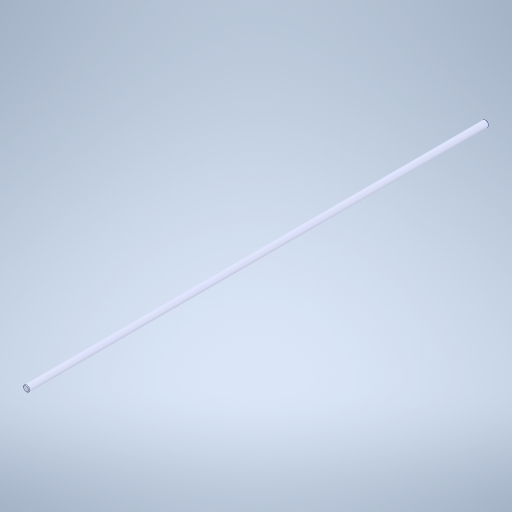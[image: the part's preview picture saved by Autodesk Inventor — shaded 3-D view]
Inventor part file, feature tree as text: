
AUTODESK INVENTOR PART (.ipt)
format: ipt  version: 2023 (Build 270158000, 158)  size: 261,120 bytes
history: mixed  units: in
note: dims shown in document units (in); Inventor stores cm internally (conversion verified against a paired STEP export)
features: chamfer x1, imported_body x1
ambient origin geometry x8: Origin, YZ Plane, XZ Plane, XY Plane, X Axis, Y Axis, Z Axis, Center Point
bodies: Solid1 (imported_parasolid)
feature tree (2):
  chamfer  "Chamfer1"  [1 undecoded]
  imported_body  NMx_Import_Brep_tag  [imported B-rep: ~5 faces, bbox_mm=[0.8, 0.0, 600.0]]
note: 1 required parameter value undecoded (feature->parameter linkage not recoverable at this tier; creation-order binding heuristic only, values carry confidence <= 0.55)
